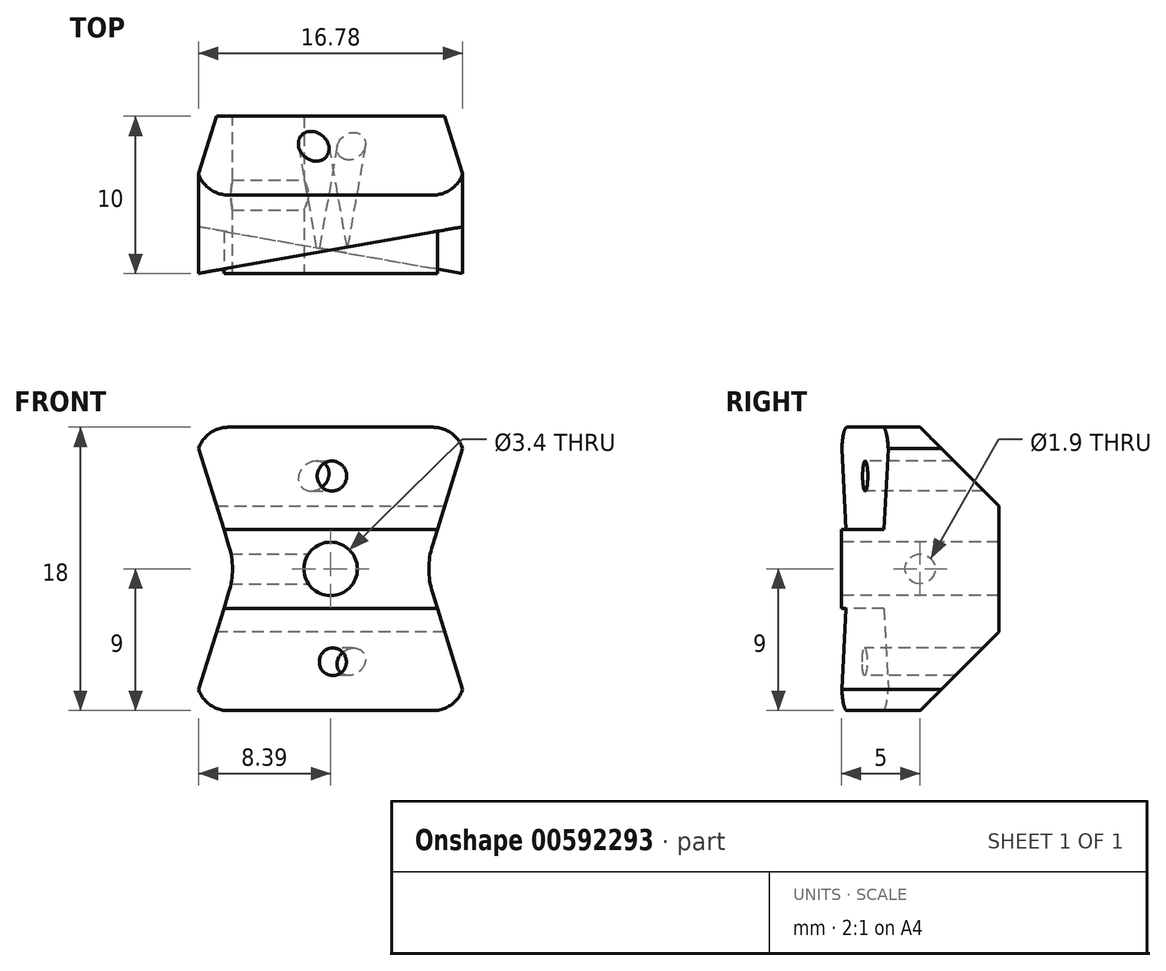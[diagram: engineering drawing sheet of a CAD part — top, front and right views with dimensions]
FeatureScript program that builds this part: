
annotation { "Feature Type Name" : "Feature", "Feature Type Description" : "" }
export const myFeature = defineFeature(function(context is Context, id is Id, definition is map)
    precondition{}
    {
        {
            var Q0;
            Q0=qCreatedBy(makeId("Front.planeOp"),FACE);
            var sketch = newSketch(context, id + "F0", { "sketchPlane" : qUnion([Q0])});
            skLineSegment(sketch, "E0.bottom", {"start": v(8.5, 9) * mm, "end": v(-8.5, 9) * mm});
            skLineSegment(sketch, "E0.top", {"start": v(8.5, -9) * mm, "end": v(-8.5, -9) * mm});
            skLineSegment(sketch, "E0.left", {"start": v(8.5, 9) * mm, "end": v(8.5, -9) * mm});
            skLineSegment(sketch, "E0.right", {"start": v(-8.5, 9) * mm, "end": v(-8.5, -9) * mm});
            skPoint(sketch, "E0.middle", {"position": v(0, 0) * mm});
            skSolve(sketch);
        }
        {
            var Q0;
            Q0 = qSketchRegion(id + "F0", true);
            extrude(context, id + "F1", {"entities" : qUnion([Q0]), "depth" : 10 * mm, "offsetDistance" : 25 * mm});
        }
        {
            var Q0;
            Q0=makeQuery(id+"F1.opExtrude","CAP_FACE",FACE,{"disambiguationData":[OSD([sQuery(id+"F0.wireOp",EDGE,"E0.bottom"),sQuery(id+"F0.wireOp",EDGE,"E0.top"),sQuery(id+"F0.wireOp",EDGE,"E0.left"),sQuery(id+"F0.wireOp",EDGE,"E0.right")])],"isStart":false});
            var sketch = newSketch(context, id + "F2", { "sketchPlane" : qUnion([Q0])});
            skCircle(sketch, "E1", {"center": v(0, 0) * mm, "radius": 1.7 * mm});
            skSolve(sketch);
        }
        {
            var Q0;
            Q0 = qSketchRegion(id + "F2", true);
            extrude(context, id + "F3", {"entities" : qUnion([Q0]), "operationType" : NewBodyOperationType.REMOVE, "oppositeDirection" : true, "depth" : 25 * mm, "offsetDistance" : 25 * mm});
        }
        {
            var Q0;
            Q0=makeQuery(id+"F1.opExtrude","SWEPT_FACE",FACE,{"disambiguationData":[OSD([sQuery(id+"F0.wireOp",EDGE,"E0.top")])]});
            var sketch = newSketch(context, id + "F4", { "sketchPlane" : qUnion([Q0])});
            skLineSegment(sketch, "E2", {"start": v(-8.5, 10) * mm, "end": v(-8.5, 7) * mm});
            skLineSegment(sketch, "E3", {"start": v(-8.5, 7) * mm, "end": v(8.5, 10) * mm});
            skLineSegment(sketch, "E4", {"start": v(8.5, 10) * mm, "end": v(8.5, 10) * mm});
            skLineSegment(sketch, "E5", {"start": v(8.5, 10) * mm, "end": v(-8.5, 10) * mm});
            skSolve(sketch);
        }
        {
            var Q0;
            Q0 = qSketchRegion(id + "F4", true);
            extrude(context, id + "F5", {"entities" : qUnion([Q0]), "operationType" : NewBodyOperationType.REMOVE, "oppositeDirection" : true, "depth" : 6.5 * mm, "offsetDistance" : 25 * mm});
        }
        {
            var Q0;
            Q0=makeQuery(id+"F1.opExtrude","SWEPT_FACE",FACE,{"disambiguationData":[OSD([sQuery(id+"F0.wireOp",EDGE,"E0.bottom")])]});
            var sketch = newSketch(context, id + "F6", { "sketchPlane" : qUnion([Q0])});
            skLineSegment(sketch, "E6", {"start": v(-8.5, -10) * mm, "end": v(8.5, -7) * mm});
            skLineSegment(sketch, "E7", {"start": v(8.5, -7) * mm, "end": v(8.5, -10) * mm});
            skLineSegment(sketch, "E8", {"start": v(8.5, -10) * mm, "end": v(-8.5, -10) * mm});
            skLineSegment(sketch, "E9", {"start": v(-8.5, -10) * mm, "end": v(-8.5, -10) * mm});
            skSolve(sketch);
        }
        {
            var Q0;
            Q0 = qSketchRegion(id + "F6", true);
            extrude(context, id + "F7", {"entities" : qUnion([Q0]), "operationType" : NewBodyOperationType.REMOVE, "oppositeDirection" : true, "depth" : 6.5 * mm, "offsetDistance" : 25 * mm});
        }
        {
            var Q0;
            Q0=makeQuery(id+"F1.opExtrude","CAP_EDGE",EDGE,{"disambiguationData":[OSD([sQuery(id+"F0.wireOp",EDGE,"E0.bottom")])],"isStart":true});
            var Q1;
            Q1=makeQuery(id+"F1.opExtrude","CAP_EDGE",EDGE,{"disambiguationData":[OSD([sQuery(id+"F0.wireOp",EDGE,"E0.top")])],"isStart":true});
            chamfer(context, id + "F8", {"entities" : qUnion([Q0, Q1]), "width" : 5 * mm, "tangentPropagation" : true});
        }
        {
            var Q0;
            Q0=makeQuery(id+"F7.boolean.opBoolean","COPY",EDGE,{"derivedFrom":makeQuery(id+"F7.opExtrude","CAP_EDGE",EDGE,{"disambiguationData":[OSD([sQuery(id+"F6.wireOp",EDGE,"E7")])],"isStart":false})});
            var Q1;
            Q1=makeQuery(id+"F5.boolean.opBoolean","COPY",EDGE,{"derivedFrom":makeQuery(id+"F5.opExtrude","CAP_EDGE",EDGE,{"disambiguationData":[OSD([sQuery(id+"F4.wireOp",EDGE,"E2")])],"isStart":false})});
            var Q2;
            Q2=makeQuery(id+"F5.boolean.opBoolean","COPY",EDGE,{"derivedFrom":makeQuery(id+"F5.opExtrude","CAP_EDGE",EDGE,{"disambiguationData":[OSD([sQuery(id+"F4.wireOp",EDGE,"E4")])],"isStart":false})});
            var Q3;
            Q3=makeQuery(id+"F7.boolean.opBoolean","COPY",EDGE,{"derivedFrom":makeQuery(id+"F7.opExtrude","CAP_EDGE",EDGE,{"disambiguationData":[OSD([sQuery(id+"F6.wireOp",EDGE,"E9")])],"isStart":false})});
            var Q4;
            Q4=makeQuery(id+"F1.opExtrude","SWEPT_EDGE",EDGE,{"disambiguationData":[OSD([sQuery(id+"F0.wireOp",EDGE,"E0.top"),sQuery(id+"F0.wireOp",EDGE,"E0.left")])]});
            var Q5;
            Q5=makeQuery(id+"F1.opExtrude","SWEPT_EDGE",EDGE,{"disambiguationData":[OSD([sQuery(id+"F0.wireOp",EDGE,"E0.top"),sQuery(id+"F0.wireOp",EDGE,"E0.right")])]});
            var Q6;
            Q6=makeQuery(id+"F1.opExtrude","SWEPT_EDGE",EDGE,{"disambiguationData":[OSD([sQuery(id+"F0.wireOp",EDGE,"E0.bottom"),sQuery(id+"F0.wireOp",EDGE,"E0.left")])]});
            var Q7;
            Q7=makeQuery(id+"F1.opExtrude","SWEPT_EDGE",EDGE,{"disambiguationData":[OSD([sQuery(id+"F0.wireOp",EDGE,"E0.bottom"),sQuery(id+"F0.wireOp",EDGE,"E0.right")])]});
            fillet(context, id + "F9", {"entities" : qUnion([Q0, Q1, Q2, Q3, Q4, Q5, Q6, Q7]), "radius" : 2 * mm, "tangentPropagation" : true, "allowEdgeOverflow" : false});
        }
        {
            var Q0;
            Q0=makeQuery(id+"F1.opExtrude","CAP_FACE",FACE,{"disambiguationData":[OSD([sQuery(id+"F0.wireOp",EDGE,"E0.bottom"),sQuery(id+"F0.wireOp",EDGE,"E0.top"),sQuery(id+"F0.wireOp",EDGE,"E0.left"),sQuery(id+"F0.wireOp",EDGE,"E0.right")])],"isStart":false});
            var sketch = newSketch(context, id + "F10", { "sketchPlane" : qUnion([Q0])});
            skLineSegment(sketch, "E10", {"start": v(-6, 0) * mm, "end": v(-8.5, 8) * mm});
            skLineSegment(sketch, "E11", {"start": v(-8.5, 8) * mm, "end": v(-8.5, -8) * mm});
            skLineSegment(sketch, "E12", {"start": v(-8.5, -8) * mm, "end": v(-6, 0) * mm});
            skLineSegment(sketch, "E13", {"start": v(8.5, 8) * mm, "end": v(6, 0) * mm});
            skLineSegment(sketch, "E14", {"start": v(6, 0) * mm, "end": v(8.5, -8) * mm});
            skLineSegment(sketch, "E15", {"start": v(8.5, -8) * mm, "end": v(8.5, 8) * mm});
            skSolve(sketch);
        }
        {
            var Q0;
            Q0 = qSketchRegion(id + "F10", true);
            extrude(context, id + "F11", {"entities" : qUnion([Q0]), "operationType" : NewBodyOperationType.REMOVE, "oppositeDirection" : true, "depth" : 25 * mm, "offsetDistance" : 25 * mm});
        }
        {
            var Q0;
            Q0=makeQuery(id+"F11.boolean.opBoolean","COPY",EDGE,{"derivedFrom":makeQuery(id+"F11.opExtrude","SWEPT_EDGE",EDGE,{"disambiguationData":[OSD([sQuery(id+"F10.wireOp",EDGE,"E10"),sQuery(id+"F10.wireOp",EDGE,"E12")])]})});
            var Q1;
            Q1=makeQuery(id+"F11.boolean.opBoolean","COPY",EDGE,{"derivedFrom":makeQuery(id+"F11.opExtrude","SWEPT_EDGE",EDGE,{"disambiguationData":[OSD([sQuery(id+"F10.wireOp",EDGE,"E13"),sQuery(id+"F10.wireOp",EDGE,"E14")])]})});
            fillet(context, id + "F12", {"entities" : qUnion([Q0, Q1]), "radius" : 5 * mm, "tangentPropagation" : true, "allowEdgeOverflow" : false});
        }
        {
            var Q0;
            Q0=makeQuery(id+"F7.boolean.opBoolean","COPY",FACE,{"derivedFrom":makeQuery(id+"F7.opExtrude","SWEPT_FACE",FACE,{"disambiguationData":[OSD([sQuery(id+"F6.wireOp",EDGE,"E6")])]})});
            var sketch = newSketch(context, id + "F13", { "sketchPlane" : qUnion([Q0])});
            skCircle(sketch, "E16", {"center": v(-1.4, 5.9) * mm, "radius": 0.95 * mm});
            skSolve(sketch);
        }
        {
            var Q0;
            Q0 = qSketchRegion(id + "F13", true);
            extrude(context, id + "F14", {"entities" : qUnion([Q0]), "operationType" : NewBodyOperationType.REMOVE, "oppositeDirection" : true, "depth" : 25 * mm, "offsetDistance" : 25 * mm});
        }
        {
            var Q0;
            Q0=makeQuery(id+"F5.boolean.opBoolean","COPY",FACE,{"derivedFrom":makeQuery(id+"F5.opExtrude","SWEPT_FACE",FACE,{"disambiguationData":[OSD([sQuery(id+"F4.wireOp",EDGE,"E3")])]})});
            var sketch = newSketch(context, id + "F15", { "sketchPlane" : qUnion([Q0])});
            skCircle(sketch, "E17", {"center": v(1.62, -5.9) * mm, "radius": 0.88 * mm});
            skPoint(sketch, "E17.centerSnap0", {"position": v(1.62, -2.5) * mm});
            skSolve(sketch);
        }
        {
            var Q0;
            Q0 = qSketchRegion(id + "F15", true);
            extrude(context, id + "F16", {"entities" : qUnion([Q0]), "operationType" : NewBodyOperationType.REMOVE, "oppositeDirection" : true, "depth" : 25 * mm, "offsetDistance" : 25 * mm});
        }
        {
            var Q0;
            Q0=qCreatedBy(makeId("Right.planeOp"),FACE);
            var sketch = newSketch(context, id + "F17", { "sketchPlane" : qUnion([Q0])});
            skCircle(sketch, "E18", {"center": v(-5, 0) * mm, "radius": 0.95 * mm});
            skSolve(sketch);
        }
        {
            var Q0;
            Q0 = qSketchRegion(id + "F17", true);
            extrude(context, id + "F18", {"entities" : qUnion([Q0]), "operationType" : NewBodyOperationType.REMOVE, "oppositeDirection" : true, "depth" : 25 * mm, "offsetDistance" : 25 * mm});
        }
    });
